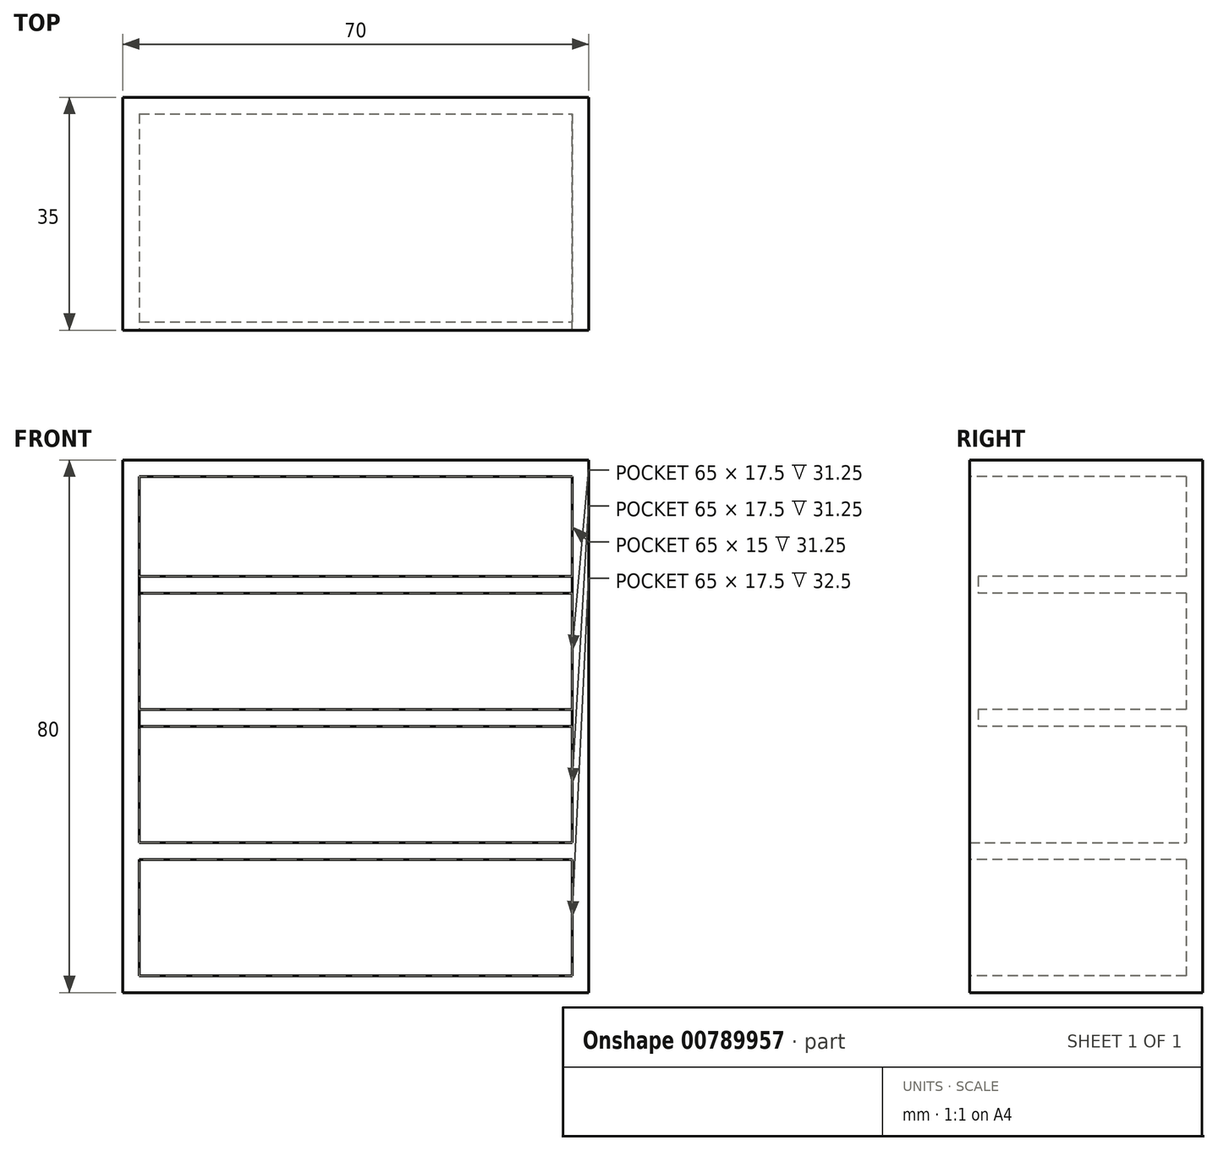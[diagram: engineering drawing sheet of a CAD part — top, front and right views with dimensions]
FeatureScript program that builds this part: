
annotation { "Feature Type Name" : "Feature", "Feature Type Description" : "" }
export const myFeature = defineFeature(function(context is Context, id is Id, definition is map)
    precondition{}
    {
        {
            var Q0;
            Q0=qCreatedBy(makeId("Top.planeOp"),FACE);
            var sketch = newSketch(context, id + "F0", { "sketchPlane" : qUnion([Q0])});
            skLineSegment(sketch, "E0.bottom", {"start": v(-35, 17.5) * mm, "end": v(35, 17.5) * mm});
            skLineSegment(sketch, "E0.top", {"start": v(-35, -17.5) * mm, "end": v(35, -17.5) * mm});
            skLineSegment(sketch, "E0.left", {"start": v(-35, 17.5) * mm, "end": v(-35, -17.5) * mm});
            skLineSegment(sketch, "E0.right", {"start": v(35, 17.5) * mm, "end": v(35, -17.5) * mm});
            skPoint(sketch, "E0.middle", {"position": v(0, 0) * mm});
            skSolve(sketch);
        }
        {
            var Q0;
            Q0=makeQuery(id+"F0.imprint","IMPRINT",FACE,{"disambiguationData":[TD([[makeQuery(id+"F0.imprint","IMPRINT",EDGE,{"derivedFrom":sQuery(id+"F0.wireOp",EDGE,"E0.bottom")}),-1.0]])]});
            extrude(context, id + "F1", {"entities" : qUnion([Q0]), "depth" : 80 * mm, "offsetDistance" : 25 * mm});
        }
        {
            var Q0;
            Q0=makeQuery(id+"F1.opExtrude","SWEPT_FACE",FACE,{"disambiguationData":[OSD([sQuery(id+"F0.wireOp",EDGE,"E0.top")])]});
            shell(context, id + "F2", {"entities" : qUnion([Q0]), "thickness" : 2.5 * mm});
        }
        {
            var Q0;
            Q0=qCreatedBy(makeId("Top.planeOp"),FACE);
            cPlane(context, id + "F3", {"entities" : qUnion([Q0]), "cplaneType" : CPlaneType.OFFSET, "offset" : 20 * mm, "width" : 150 * mm, "height" : 150 * mm});
        }
        {
            var Q0;
            Q0=qCreatedBy(id+"F3.planeOp",FACE);
            var sketch = newSketch(context, id + "F4", { "sketchPlane" : qUnion([Q0])});
            skLineSegment(sketch, "E1.0.0", {"start": v(-32.5, 15) * mm, "end": v(-32.5, -17.5) * mm});
            skLineSegment(sketch, "E1.0.1", {"start": v(-32.5, -17.5) * mm, "end": v(32.5, -17.5) * mm});
            skLineSegment(sketch, "E1.0.2", {"start": v(32.5, -17.5) * mm, "end": v(32.5, 15) * mm});
            skLineSegment(sketch, "E1.0.3", {"start": v(32.5, 15) * mm, "end": v(-32.5, 15) * mm});
            skSolve(sketch);
        }
        {
            var Q0;
            Q0=makeQuery(id+"F4.imprint","IMPRINT",FACE,{"disambiguationData":[TD([[makeQuery(id+"F4.imprint","IMPRINT",EDGE,{"derivedFrom":sQuery(id+"F4.wireOp",EDGE,"E1.0.0")}),1.0]])]});
            extrude(context, id + "F5", {"entities" : qUnion([Q0]), "operationType" : NewBodyOperationType.ADD, "depth" : 2.5 * mm, "offsetDistance" : 25 * mm});
        }
        {
            var Q0;
            Q0=qCreatedBy(makeId("Top.planeOp"),FACE);
            cPlane(context, id + "F6", {"entities" : qUnion([Q0]), "cplaneType" : CPlaneType.OFFSET, "offset" : 40 * mm, "width" : 150 * mm, "height" : 150 * mm});
        }
        {
            var Q0;
            Q0=qCreatedBy(id+"F6.planeOp",FACE);
            var sketch = newSketch(context, id + "F7", { "sketchPlane" : qUnion([Q0])});
            skLineSegment(sketch, "E2.bottom", {"start": v(-32.5, 16.25) * mm, "end": v(32.5, 16.25) * mm});
            skLineSegment(sketch, "E2.top", {"start": v(-32.5, -16.25) * mm, "end": v(32.5, -16.25) * mm});
            skLineSegment(sketch, "E2.left", {"start": v(-32.5, 16.25) * mm, "end": v(-32.5, -16.25) * mm});
            skLineSegment(sketch, "E2.right", {"start": v(32.5, 16.25) * mm, "end": v(32.5, -16.25) * mm});
            skPoint(sketch, "E2.middle", {"position": v(0, 0) * mm});
            skSolve(sketch);
        }
        {
            var Q0;
            Q0=makeQuery(id+"F7.imprint","IMPRINT",FACE,{"disambiguationData":[TD([[makeQuery(id+"F7.imprint","IMPRINT",EDGE,{"derivedFrom":sQuery(id+"F7.wireOp",EDGE,"E2.bottom")}),-1.0]])]});
            extrude(context, id + "F8", {"entities" : qUnion([Q0]), "operationType" : NewBodyOperationType.ADD, "depth" : 2.5 * mm, "offsetDistance" : 25 * mm});
        }
        {
            var Q0;
            Q0=qCreatedBy(makeId("Top.planeOp"),FACE);
            cPlane(context, id + "F9", {"entities" : qUnion([Q0]), "cplaneType" : CPlaneType.OFFSET, "offset" : 60 * mm, "width" : 150 * mm, "height" : 150 * mm});
        }
        {
            var Q0;
            Q0=qCreatedBy(id+"F9.planeOp",FACE);
            var sketch = newSketch(context, id + "F10", { "sketchPlane" : qUnion([Q0])});
            skLineSegment(sketch, "E3.bottom", {"start": v(-32.5, 16.25) * mm, "end": v(32.5, 16.25) * mm});
            skLineSegment(sketch, "E3.top", {"start": v(-32.5, -16.25) * mm, "end": v(32.5, -16.25) * mm});
            skLineSegment(sketch, "E3.left", {"start": v(-32.5, 16.25) * mm, "end": v(-32.5, -16.25) * mm});
            skLineSegment(sketch, "E3.right", {"start": v(32.5, 16.25) * mm, "end": v(32.5, -16.25) * mm});
            skPoint(sketch, "E3.middle", {"position": v(0, 0) * mm});
            skSolve(sketch);
        }
        {
            var Q0;
            Q0 = qSketchRegion(id + "F10", true);
            extrude(context, id + "F11", {"entities" : qUnion([Q0]), "operationType" : NewBodyOperationType.ADD, "depth" : 2.5 * mm, "offsetDistance" : 25 * mm});
        }
    });
